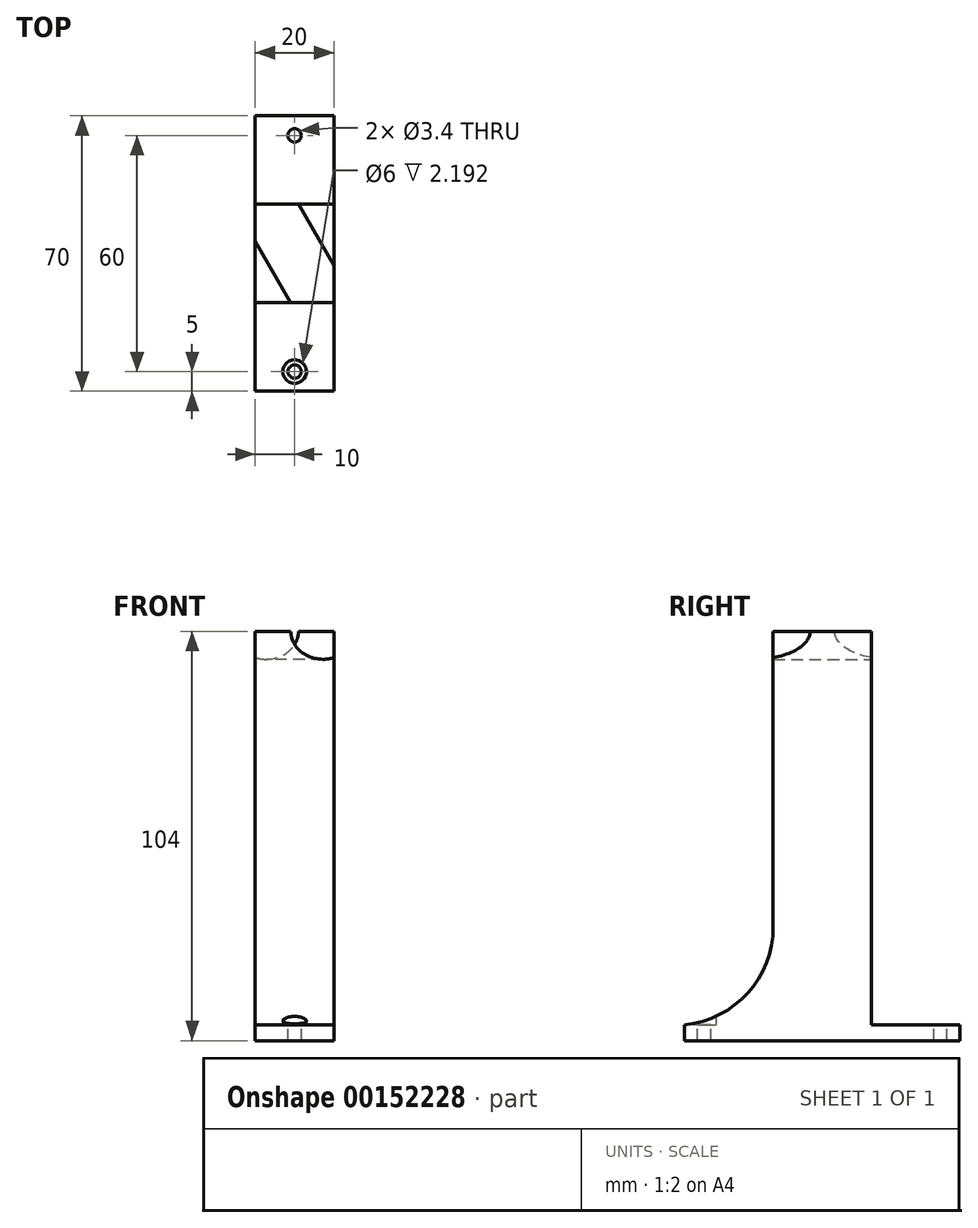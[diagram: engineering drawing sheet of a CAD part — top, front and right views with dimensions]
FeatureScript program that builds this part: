
annotation { "Feature Type Name" : "Feature", "Feature Type Description" : "" }
export const myFeature = defineFeature(function(context is Context, id is Id, definition is map)
    precondition{}
    {
        {
            var Q0;
            Q0=qCreatedBy(makeId("Top.planeOp"),FACE);
            var sketch = newSketch(context, id + "F0", { "sketchPlane" : qUnion([Q0])});
            skLineSegment(sketch, "E0.bottom", {"start": v(10, 35) * mm, "end": v(-10, 35) * mm});
            skLineSegment(sketch, "E0.top", {"start": v(10, -35) * mm, "end": v(-10, -35) * mm});
            skLineSegment(sketch, "E0.left", {"start": v(10, 35) * mm, "end": v(10, -35) * mm});
            skLineSegment(sketch, "E0.right", {"start": v(-10, 35) * mm, "end": v(-10, -35) * mm});
            skPoint(sketch, "E0.middle", {"position": v(0, 0) * mm});
            skLineSegment(sketch, "E1.bottom", {"start": v(10, -35) * mm, "end": v(0, -35) * mm, "construction": true});
            skLineSegment(sketch, "E1.top", {"start": v(10, -30) * mm, "end": v(0, -30) * mm, "construction": true});
            skLineSegment(sketch, "E1.left", {"start": v(10, -35) * mm, "end": v(10, -30) * mm, "construction": true});
            skLineSegment(sketch, "E1.right", {"start": v(0, -35) * mm, "end": v(0, -30) * mm, "construction": true});
            skCircle(sketch, "E2", {"center": v(0, -30) * mm, "radius": 1.7 * mm});
            skLineSegment(sketch, "E3.bottom", {"start": v(10, 35) * mm, "end": v(0, 35) * mm, "construction": true});
            skLineSegment(sketch, "E3.top", {"start": v(10, 30) * mm, "end": v(0, 30) * mm, "construction": true});
            skLineSegment(sketch, "E3.left", {"start": v(10, 35) * mm, "end": v(10, 30) * mm, "construction": true});
            skLineSegment(sketch, "E3.right", {"start": v(0, 35) * mm, "end": v(0, 30) * mm, "construction": true});
            skCircle(sketch, "E4", {"center": v(0, 30) * mm, "radius": 1.7 * mm});
            skLineSegment(sketch, "E5", {"start": v(0, 0) * mm, "end": v(-4.23, 7.33) * mm, "construction": true});
            skLineSegment(sketch, "E6", {"start": v(0, 0) * mm, "end": v(6.15, 3.55) * mm});
            skLineSegment(sketch, "E7", {"start": v(0, 0) * mm, "end": v(-6.15, -3.55) * mm});
            skLineSegment(sketch, "E8", {"start": v(-6.15, -3.55) * mm, "end": v(-14.4, 10.76) * mm});
            skLineSegment(sketch, "E9", {"start": v(6.15, 3.55) * mm, "end": v(-12.4, 35.69) * mm});
            skLineSegment(sketch, "E10", {"start": v(6.15, 3.55) * mm, "end": v(15.22, -12.17) * mm});
            skLineSegment(sketch, "E11", {"start": v(-6.15, -3.55) * mm, "end": v(14.75, -39.75) * mm});
            skLineSegment(sketch, "E12", {"start": v(6.15, 3.55) * mm, "end": v(10, 5.77) * mm});
            skLineSegment(sketch, "E13", {"start": v(-6.15, -3.55) * mm, "end": v(-10, -5.77) * mm});
            skLineSegment(sketch, "E14", {"start": v(-10, -5.77) * mm, "end": v(-17.19, 6.68) * mm});
            skLineSegment(sketch, "E15", {"start": v(-17.19, 6.68) * mm, "end": v(-3.7, -16.67) * mm});
            skLineSegment(sketch, "E16", {"start": v(10, 5.77) * mm, "end": v(4.32, 15.6) * mm});
            skLineSegment(sketch, "E17", {"start": v(4.32, 15.6) * mm, "end": v(18.47, -8.9) * mm});
            skLineSegment(sketch, "E18.bottom", {"start": v(10, 12.5) * mm, "end": v(-10, 12.5) * mm});
            skLineSegment(sketch, "E18.top", {"start": v(10, -12.5) * mm, "end": v(-10, -12.5) * mm});
            skLineSegment(sketch, "E18.left", {"start": v(10, 12.5) * mm, "end": v(10, -12.5) * mm});
            skLineSegment(sketch, "E18.right", {"start": v(-10, 12.5) * mm, "end": v(-10, -12.5) * mm});
            skCircle(sketch, "E19", {"center": v(0, -30) * mm, "radius": 3 * mm});
            skCircle(sketch, "E20", {"center": v(0, 30) * mm, "radius": 3 * mm});
            skSolve(sketch);
        }
        {
            var Q0;
            {var subQ0=sQuery(id+"F0.wireOp",EDGE,"E13");var subQ5=sQuery(id+"F0.wireOp",EDGE,"E18.top");var subQ8=makeQuery(id+"F0.imprint","IMPRINT",EDGE,{"derivedFrom":subQ0});var subQ10=sQuery(id+"F0.wireOp",EDGE,"E0.right");var subQ15=sQuery(id+"F0.wireOp",EDGE,"E0.left");var subQ16=makeQuery(id+"F0.imprint","INTERSECT",VERTEX,{"derivedFrom":[subQ15,subQ5]});var subQ21=sQuery(id+"F0.wireOp",EDGE,"E12");var subQ23=sQuery(id+"F0.wireOp",EDGE,"E9");var subQ24=sQuery(id+"F0.wireOp",EDGE,"E6");var subQ28=makeQuery(id+"F0.imprint","IMPRINT",EDGE,{"derivedFrom":subQ24});var subQ29=makeQuery(id+"F0.imprint","INTERSECT",VERTEX,{"derivedFrom":[subQ10,subQ23]});var subQ30=sQuery(id+"F0.wireOp",EDGE,"E18.bottom");var subQ35=sQuery(id+"F0.wireOp",EDGE,"E0.top");var subQ36=makeQuery(id+"F0.imprint","INTERSECT",VERTEX,{"derivedFrom":[subQ10,subQ5]});var subQ37=makeQuery(id+"F0.imprint","IMPRINT",EDGE,{"disambiguationData":[TD([[subQ36,1.0]])],"derivedFrom":subQ5});var subQ39=makeQuery(id+"F0.imprint","IMPRINT",EDGE,{"derivedFrom":subQ21});var subQ40=sQuery(id+"F0.wireOp",EDGE,"E16");var subQ41=makeQuery(id+"F0.imprint","INTERSECT",VERTEX,{"derivedFrom":[subQ40,subQ30]});var subQ46=makeQuery(id+"F0.imprint","IMPRINT",EDGE,{"disambiguationData":[TD([[subQ41,1.0]])],"derivedFrom":subQ30});var subQ47=sQuery(id+"F0.wireOp",EDGE,"E0.bottom");Q0=qUnion([makeQuery(id+"F0.imprint","IMPRINT",FACE,{"disambiguationData":[TD([[subQ39,-1.0]])]}),makeQuery(id+"F0.imprint","IMPRINT",FACE,{"disambiguationData":[TD([[subQ28,1.0]])]}),makeQuery(id+"F0.imprint","IMPRINT",FACE,{"disambiguationData":[TD([[subQ8,-1.0]])]}),makeQuery(id+"F0.imprint","IMPRINT",FACE,{"disambiguationData":[TD([[makeQuery(id+"F0.imprint","IMPRINT",EDGE,{"derivedFrom":subQ47}),1.0]])]}),makeQuery(id+"F0.imprint","IMPRINT",FACE,{"disambiguationData":[TD([[subQ46,1.0]])]}),makeQuery(id+"F0.imprint","IMPRINT",FACE,{"disambiguationData":[TD([[subQ39,1.0]])]}),makeQuery(id+"F0.imprint","IMPRINT",FACE,{"disambiguationData":[TD([[subQ37,-1.0]])]}),makeQuery(id+"F0.imprint","IMPRINT",FACE,{"disambiguationData":[TD([[makeQuery(id+"F0.imprint","IMPRINT",EDGE,{"derivedFrom":subQ35}),-1.0]])]}),makeQuery(id+"F0.imprint","IMPRINT",FACE,{"disambiguationData":[TD([[makeQuery(id+"F0.imprint","IMPRINT",EDGE,{"disambiguationData":[TD([[subQ29,-1.0]])],"derivedFrom":subQ10}),1.0]])]}),makeQuery(id+"F0.imprint","IMPRINT",FACE,{"disambiguationData":[TD([[subQ28,-1.0]])]}),makeQuery(id+"F0.imprint","IMPRINT",FACE,{"disambiguationData":[TD([[makeQuery(id+"F0.imprint","IMPRINT",EDGE,{"disambiguationData":[TD([[subQ16,-1.0]])],"derivedFrom":subQ15}),-1.0]])]}),makeQuery(id+"F0.imprint","IMPRINT",FACE,{"disambiguationData":[TD([[subQ8,1.0]])]})]);}
            var Q1;
            Q1=makeQuery(id+"F0.imprint","IMPRINT",FACE,{"disambiguationData":[TD([[makeQuery(id+"F0.imprint","IMPRINT",EDGE,{"derivedFrom":sQuery(id+"F0.wireOp",EDGE,"E2")}),-1.0]])]});
            var Q2;
            Q2=makeQuery(id+"F0.imprint","IMPRINT",FACE,{"disambiguationData":[TD([[makeQuery(id+"F0.imprint","IMPRINT",EDGE,{"derivedFrom":sQuery(id+"F0.wireOp",EDGE,"E4")}),-1.0]])]});
            extrude(context, id + "F1", {"entities" : qUnion([Q0, Q1, Q2]), "oppositeDirection" : true, "depth" : 4 * mm, "offsetDistance" : 25 * mm});
        }
        {
            var Q0;
            {var subQ0=sQuery(id+"F0.wireOp",EDGE,"E13");Q0=makeQuery(id+"F0.imprint","IMPRINT",FACE,{"disambiguationData":[TD([[makeQuery(id+"F0.imprint","IMPRINT",EDGE,{"derivedFrom":subQ0}),1.0]])]});}
            var Q1;
            {var subQ3=sQuery(id+"F0.wireOp",EDGE,"E13");Q1=makeQuery(id+"F0.imprint","IMPRINT",FACE,{"disambiguationData":[TD([[makeQuery(id+"F0.imprint","IMPRINT",EDGE,{"derivedFrom":subQ3}),-1.0]])]});}
            var Q2;
            {var subQ8=sQuery(id+"F0.wireOp",EDGE,"E6");Q2=makeQuery(id+"F0.imprint","IMPRINT",FACE,{"disambiguationData":[TD([[makeQuery(id+"F0.imprint","IMPRINT",EDGE,{"derivedFrom":subQ8}),1.0]])]});}
            var Q3;
            {var subQ2=sQuery(id+"F0.wireOp",EDGE,"E6");Q3=makeQuery(id+"F0.imprint","IMPRINT",FACE,{"disambiguationData":[TD([[makeQuery(id+"F0.imprint","IMPRINT",EDGE,{"derivedFrom":subQ2}),-1.0]])]});}
            var Q4;
            {var subQ3=sQuery(id+"F0.wireOp",EDGE,"E12");Q4=makeQuery(id+"F0.imprint","IMPRINT",FACE,{"disambiguationData":[TD([[makeQuery(id+"F0.imprint","IMPRINT",EDGE,{"derivedFrom":subQ3}),-1.0]])]});}
            var Q5;
            {var subQ0=sQuery(id+"F0.wireOp",EDGE,"E12");Q5=makeQuery(id+"F0.imprint","IMPRINT",FACE,{"disambiguationData":[TD([[makeQuery(id+"F0.imprint","IMPRINT",EDGE,{"derivedFrom":subQ0}),1.0]])]});}
            var Q6;
            {var subQ0=sQuery(id+"F0.wireOp",EDGE,"E16");var subQ3=sQuery(id+"F0.wireOp",EDGE,"E18.bottom");var subQ5=makeQuery(id+"F0.imprint","INTERSECT",VERTEX,{"derivedFrom":[subQ0,subQ3]});Q6=makeQuery(id+"F0.imprint","IMPRINT",FACE,{"disambiguationData":[TD([[makeQuery(id+"F0.imprint","IMPRINT",EDGE,{"disambiguationData":[TD([[subQ5,1.0]])],"derivedFrom":subQ3}),1.0]])]});}
            var Q7;
            {var subQ0=sQuery(id+"F0.wireOp",EDGE,"E18.top");var subQ1=sQuery(id+"F0.wireOp",EDGE,"E0.right");var subQ2=makeQuery(id+"F0.imprint","INTERSECT",VERTEX,{"derivedFrom":[subQ1,subQ0]});Q7=makeQuery(id+"F0.imprint","IMPRINT",FACE,{"disambiguationData":[TD([[makeQuery(id+"F0.imprint","IMPRINT",EDGE,{"disambiguationData":[TD([[subQ2,1.0]])],"derivedFrom":subQ0}),-1.0]])]});}
            extrude(context, id + "F2", {"entities" : qUnion([Q0, Q1, Q2, Q3, Q4, Q5, Q6, Q7]), "operationType" : NewBodyOperationType.ADD, "depth" : 100 * mm, "offsetDistance" : 25 * mm});
        }
        {
            var Q0;
            Q0=sQuery(id+"F0.wireOp",EDGE,"E6");
            cPlane(context, id + "F3", {"entities" : qUnion([Q0]), "cplaneType" : CPlaneType.LINE_ANGLE, "offset" : 25 * mm, "angle" : 0 * degree, "width" : 150 * mm, "height" : 150 * mm});
        }
        {
            var Q0;
            Q0=qCreatedBy(id+"F3.planeOp",FACE);
            var sketch = newSketch(context, id + "F4", { "sketchPlane" : qUnion([Q0])});
            skLineSegment(sketch, "E21", {"start": v(0, 0) * mm, "end": v(0, 100) * mm});
            skCircle(sketch, "E22", {"center": v(0, 100) * mm, "radius": 7.1 * mm});
            skSolve(sketch);
        }
        {
            var Q0;
            Q0=makeQuery(id+"F4.imprint","IMPRINT",FACE,{"disambiguationData":[TD([[makeQuery(id+"F4.imprint","IMPRINT",EDGE,{"derivedFrom":sQuery(id+"F4.wireOp",EDGE,"E22")}),1.0]])]});
            extrude(context, id + "F5", {"entities" : qUnion([Q0]), "operationType" : NewBodyOperationType.REMOVE, "endBound" : BoundingType.SYMMETRIC, "oppositeDirection" : true, "depth" : 40 * mm, "offsetDistance" : 25 * mm});
        }
        {
            var Q0;
            Q0=makeQuery(id+"F2.opExtrude","CAP_EDGE",EDGE,{"disambiguationData":[OSD([sQuery(id+"F0.wireOp",EDGE,"E18.top")])],"isStart":true});
            var Q1;
            Q1=makeQuery(id+"F2.opExtrude","CAP_EDGE",EDGE,{"disambiguationData":[OSD([sQuery(id+"F0.wireOp",EDGE,"E18.bottom")])],"isStart":true});
            fillet(context, id + "F6", {"entities" : qUnion([Q0, Q1]), "radius" : 25 * mm, "tangentPropagation" : true, "allowEdgeOverflow" : false});
        }
        {
            var Q0;
            Q0=makeQuery(id+"F0.imprint","IMPRINT",FACE,{"disambiguationData":[TD([[makeQuery(id+"F0.imprint","IMPRINT",EDGE,{"derivedFrom":sQuery(id+"F0.wireOp",EDGE,"E2")}),-1.0]])]});
            var Q1;
            Q1=makeQuery(id+"F0.imprint","IMPRINT",FACE,{"disambiguationData":[TD([[makeQuery(id+"F0.imprint","IMPRINT",EDGE,{"derivedFrom":sQuery(id+"F0.wireOp",EDGE,"E4")}),-1.0]])]});
            extrude(context, id + "F7", {"entities" : qUnion([Q0, Q1]), "operationType" : NewBodyOperationType.REMOVE, "depth" : 25 * mm, "offsetDistance" : 25 * mm});
        }
    });
